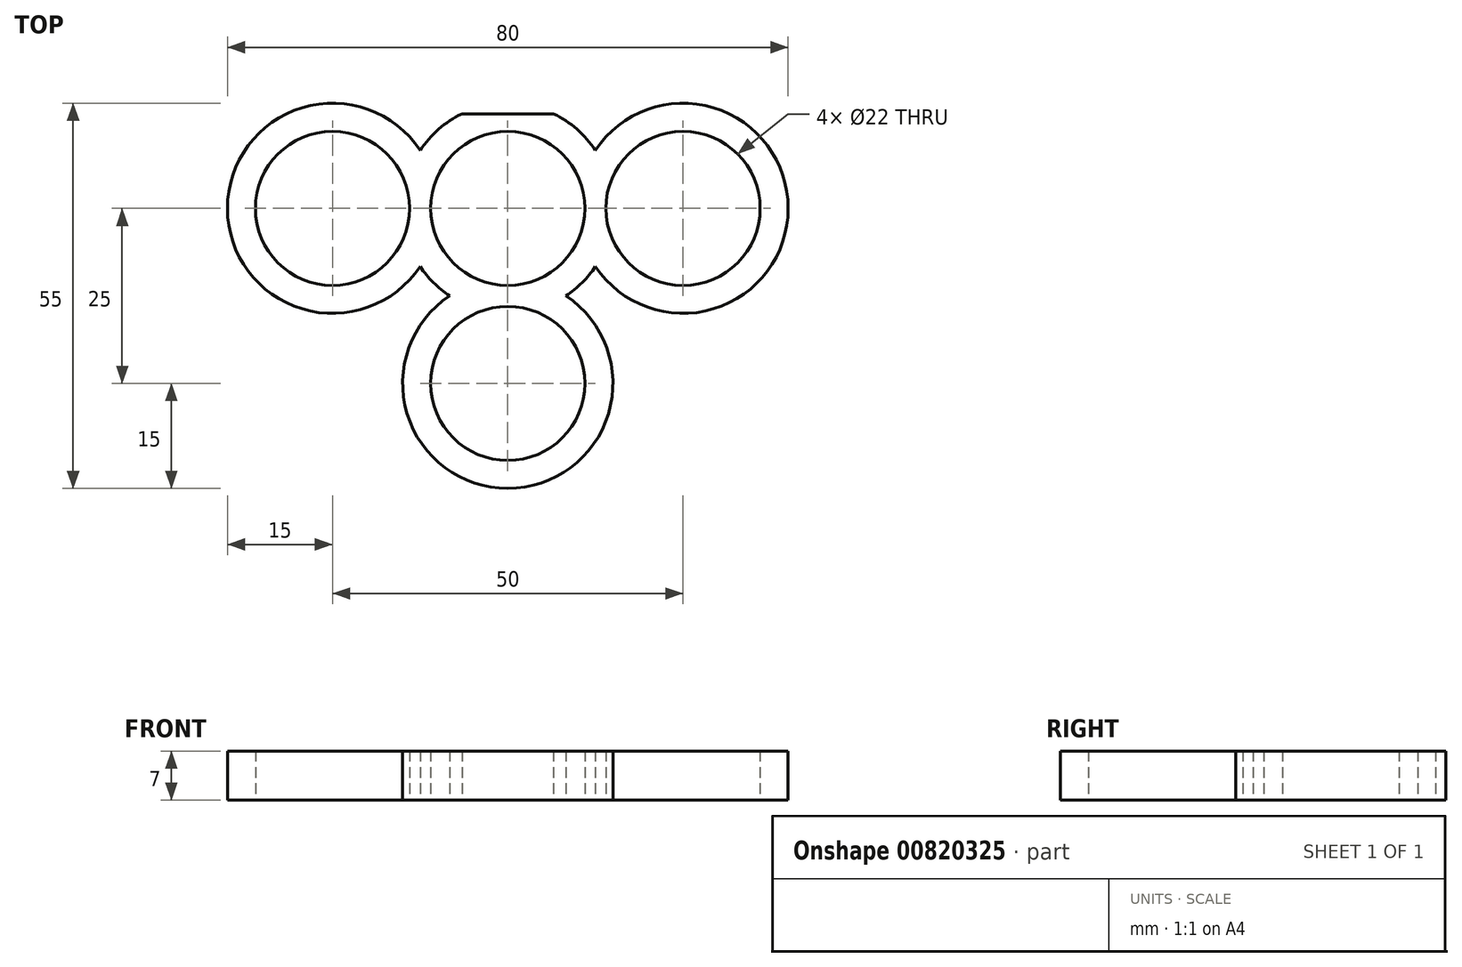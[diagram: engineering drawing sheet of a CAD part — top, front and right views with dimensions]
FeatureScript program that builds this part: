
annotation { "Feature Type Name" : "Feature", "Feature Type Description" : "" }
export const myFeature = defineFeature(function(context is Context, id is Id, definition is map)
    precondition{}
    {
        {
            var Q0;
            Q0=qCreatedBy(makeId("Top.planeOp"),FACE);
            var sketch = newSketch(context, id + "F0", { "sketchPlane" : qUnion([Q0])});
            skArc(sketch, "E0", {"start": v(0, 11) * mm, "mid": v(-11, 0) * mm, "end": v(0, -11) * mm});
            skArc(sketch, "E1", {"start": v(-12.5, -8.3) * mm, "mid": v(-10.6, -10.6) * mm, "end": v(-8.3, -12.5) * mm});
            skLineSegment(sketch, "E2", {"start": v(-10, 0) * mm, "end": v(-11, 0) * mm});
            skCircle(sketch, "E3", {"center": v(-25, 0) * mm, "radius": 11 * mm});
            skArc(sketch, "E4", {"start": v(-12.5, 8.3) * mm, "mid": v(-40, 0) * mm, "end": v(-12.5, -8.3) * mm});
            skLineSegment(sketch, "E5.trimOffspring", {"start": v(-14, 0) * mm, "end": v(-15, 0) * mm});
            skLineSegment(sketch, "E6", {"start": v(0, 15) * mm, "end": v(0, -11) * mm});
            skLineSegment(sketch, "E7", {"start": v(0, 15) * mm, "end": v(0, -15) * mm});
            skArc(sketch, "E8.trimOffspring", {"start": v(-6.54, 13.5) * mm, "mid": v(-9.87, 11.3) * mm, "end": v(-12.5, 8.3) * mm});
            skLineSegment(sketch, "E9.MirrorCS", {"start": v(10, 0) * mm, "end": v(11, 0) * mm});
            skLineSegment(sketch, "E10.MirrorCS", {"start": v(14, 0) * mm, "end": v(15, 0) * mm});
            skArc(sketch, "E11.MirrorCS", {"start": v(12.5, -8.3) * mm, "mid": v(10.6, -10.6) * mm, "end": v(8.3, -12.5) * mm});
            skArc(sketch, "E12.MirrorCS", {"start": v(6.54, 13.5) * mm, "mid": v(9.87, 11.3) * mm, "end": v(12.5, 8.3) * mm});
            skArc(sketch, "E13.MirrorCS", {"start": v(12.5, 8.3) * mm, "mid": v(40, 0) * mm, "end": v(12.5, -8.3) * mm});
            skCircle(sketch, "E14.MirrorC", {"center": v(25, 0) * mm, "radius": 11 * mm});
            skArc(sketch, "E15.MirrorCS", {"start": v(0, 11) * mm, "mid": v(11, 0) * mm, "end": v(0, -11) * mm});
            skLineSegment(sketch, "E16", {"start": v(0, 0) * mm, "end": v(0, -25) * mm});
            skCircle(sketch, "E17", {"center": v(0, -25) * mm, "radius": 11 * mm});
            skArc(sketch, "E18", {"start": v(-8.3, -12.5) * mm, "mid": v(0, -40) * mm, "end": v(8.3, -12.5) * mm});
            skPoint(sketch, "E19.trimOffspring.end.orphan", {"position": v(0, -15) * mm});
            skLineSegment(sketch, "E20", {"start": v(0, 2) * mm, "end": v(0, 27) * mm});
            skPoint(sketch, "E21.orphan", {"position": v(0, 15) * mm});
            skLineSegment(sketch, "E22", {"start": v(-6.54, 13.5) * mm, "end": v(6.54, 13.5) * mm});
            skPoint(sketch, "E23.visualSharp", {"position": v(-6.54, 13.5) * mm});
            skLineSegment(sketch, "E23.filletArc", {"start": v(-6.54, 13.5) * mm, "end": v(-6.54, 13.5) * mm});
            skSolve(sketch);
        }
        {
            var Q0;
            Q0 = qSketchRegion(id + "F0", true);
            extrude(context, id + "F1", {"entities" : qUnion([Q0]), "depth" : 7 * mm, "offsetDistance" : 25 * mm});
        }
    });
